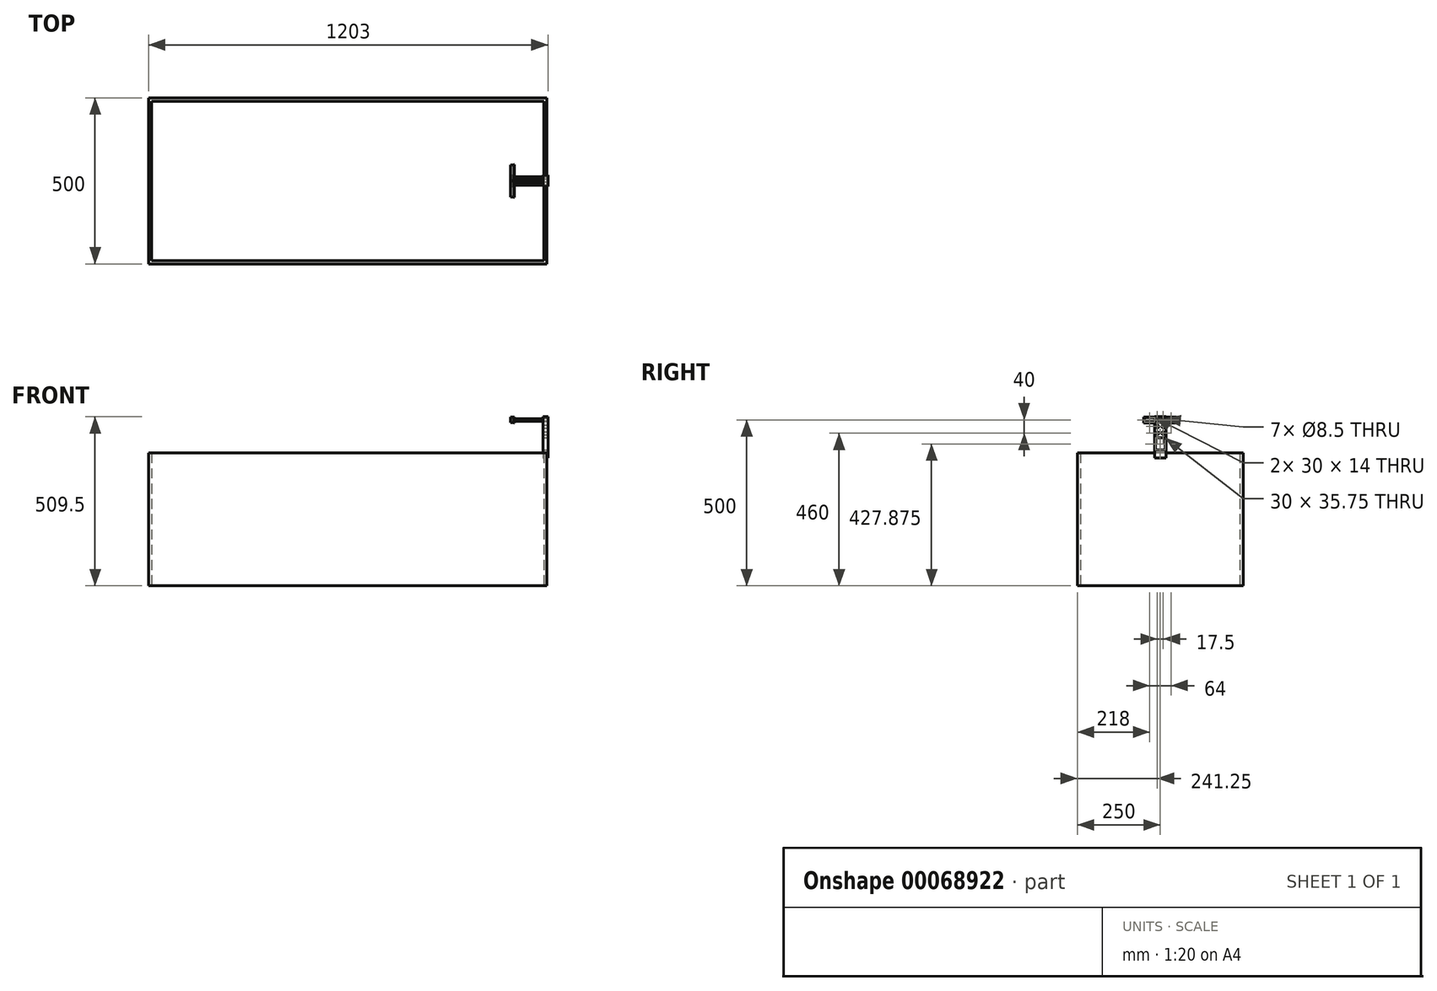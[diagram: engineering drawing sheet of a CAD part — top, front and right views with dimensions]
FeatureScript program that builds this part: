
annotation { "Feature Type Name" : "Feature", "Feature Type Description" : "" }
export const myFeature = defineFeature(function(context is Context, id is Id, definition is map)
    precondition{}
    {
        {
            var Q0;
            Q0=qCreatedBy(makeId("Right.planeOp"),FACE);
            var sketch = newSketch(context, id + "F0", { "sketchPlane" : qUnion([Q0])});
            skLineSegment(sketch, "E0.rect.bottom", {"start": v(-49.5, 9) * mm, "end": v(49.5, 9) * mm});
            skLineSegment(sketch, "E0.rect.top", {"start": v(-49.5, -9) * mm, "end": v(49.5, -9) * mm});
            skLineSegment(sketch, "E0.rect.left", {"start": v(-49.5, 9) * mm, "end": v(-49.5, -9) * mm});
            skLineSegment(sketch, "E0.rect.right", {"start": v(49.5, 9) * mm, "end": v(49.5, -9) * mm});
            skLineSegment(sketch, "E1.bottom", {"start": v(-49.5, -9) * mm, "end": v(0, -9) * mm, "construction": true});
            skLineSegment(sketch, "E1.top", {"start": v(-49.5, 9) * mm, "end": v(0, 9) * mm, "construction": true});
            skLineSegment(sketch, "E2", {"start": v(0, 9) * mm, "end": v(0, -9) * mm, "construction": true});
            skPoint(sketch, "E3.middle", {"position": v(0, 0) * mm});
            skLineSegment(sketch, "E4.bottom", {"start": v(-48, 8) * mm, "end": v(-16, 8) * mm});
            skLineSegment(sketch, "E4.top", {"start": v(-48, -8) * mm, "end": v(-16, -8) * mm});
            skLineSegment(sketch, "E4.left", {"start": v(-48, 8) * mm, "end": v(-48, -8) * mm});
            skLineSegment(sketch, "E5.MirrorCS", {"start": v(48, 8) * mm, "end": v(48, -8) * mm});
            skLineSegment(sketch, "E6.MirrorCS", {"start": v(48, 8) * mm, "end": v(16, 8) * mm});
            skLineSegment(sketch, "E7.MirrorCS", {"start": v(48, -8) * mm, "end": v(16, -8) * mm});
            skLineSegment(sketch, "E8.bottom", {"start": v(50, 9.5) * mm, "end": v(-50, 9.5) * mm});
            skLineSegment(sketch, "E8.top", {"start": v(50, -9.5) * mm, "end": v(-50, -9.5) * mm});
            skLineSegment(sketch, "E8.left", {"start": v(50, 9.5) * mm, "end": v(50, -9.5) * mm});
            skLineSegment(sketch, "E8.right", {"start": v(-50, 9.5) * mm, "end": v(-50, -9.5) * mm});
            skCircle(sketch, "E9", {"center": v(-8.75, 0) * mm, "radius": 4.25 * mm});
            skCircle(sketch, "E10.MirrorC", {"center": v(8.75, 0) * mm, "radius": 4.25 * mm});
            skLineSegment(sketch, "E11.bottom", {"start": v(0.75, 9.5) * mm, "end": v(-0.75, 9.5) * mm});
            skLineSegment(sketch, "E11.top", {"start": v(0.75, -9.5) * mm, "end": v(-0.75, -9.5) * mm});
            skLineSegment(sketch, "E11.left", {"start": v(0.75, 9.5) * mm, "end": v(0.75, -9.5) * mm});
            skLineSegment(sketch, "E11.right", {"start": v(-0.75, 9.5) * mm, "end": v(-0.75, -9.5) * mm});
            skLineSegment(sketch, "E12.0", {"start": v(47, 7) * mm, "end": v(17, 7) * mm});
            skLineSegment(sketch, "E12.1", {"start": v(47, 7) * mm, "end": v(47, -7) * mm});
            skLineSegment(sketch, "E12.2", {"start": v(47, -7) * mm, "end": v(17, -7) * mm});
            skLineSegment(sketch, "E12.3", {"start": v(17, 7) * mm, "end": v(17, -7) * mm});
            skLineSegment(sketch, "E13.MirrorCS", {"start": v(-47, 7) * mm, "end": v(-17, 7) * mm});
            skLineSegment(sketch, "E14.MirrorCS", {"start": v(-17, 7) * mm, "end": v(-17, -7) * mm});
            skLineSegment(sketch, "E15.MirrorCS", {"start": v(-47, -7) * mm, "end": v(-17, -7) * mm});
            skLineSegment(sketch, "E16.MirrorCS", {"start": v(-47, 7) * mm, "end": v(-47, -7) * mm});
            skLineSegment(sketch, "E17.bottom", {"start": v(-13, -8) * mm, "end": v(13, -8) * mm});
            skLineSegment(sketch, "E17.top", {"start": v(-13, 8) * mm, "end": v(13, 8) * mm});
            skLineSegment(sketch, "E18", {"start": v(-16, -8) * mm, "end": v(-13, -8) * mm});
            skLineSegment(sketch, "E19", {"start": v(-16, 8) * mm, "end": v(-13, 8) * mm});
            skLineSegment(sketch, "E20", {"start": v(13, -8) * mm, "end": v(16, -8) * mm});
            skLineSegment(sketch, "E21", {"start": v(13, 8) * mm, "end": v(16, 8) * mm});
            skPoint(sketch, "E3.left.end.orphan", {"position": v(-13, -6) * mm});
            skPoint(sketch, "E22.trimOffspring.start.orphan", {"position": v(-13, 6) * mm});
            skPoint(sketch, "E3.right.end.orphan", {"position": v(13, -6) * mm});
            skPoint(sketch, "E3.right.start.orphan", {"position": v(13, 6) * mm});
            skSolve(sketch);
        }
        {
            var Q0;
            Q0=makeQuery(id+"F0.imprint","IMPRINT",FACE,{"disambiguationData":[TD([[makeQuery(id+"F0.imprint","IMPRINT",EDGE,{"derivedFrom":sQuery(id+"F0.wireOp",EDGE,"E0.rect.bottom")}),-1.0]])]});
            var Q1;
            Q1=makeQuery(id+"F0.imprint","IMPRINT",FACE,{"disambiguationData":[TD([[makeQuery(id+"F0.imprint","IMPRINT",EDGE,{"derivedFrom":sQuery(id+"F0.wireOp",EDGE,"E3.bottom")}),-1.0]])]});
            var Q2;
            {var subQ0=sQuery(id+"F0.wireOp",EDGE,"E11.right");var subQ1=sQuery(id+"F0.wireOp",EDGE,"E0.rect.top");var subQ2=makeQuery(id+"F0.imprint","INTERSECT",VERTEX,{"derivedFrom":[subQ1,subQ0]});Q2=makeQuery(id+"F0.imprint","IMPRINT",FACE,{"disambiguationData":[TD([[makeQuery(id+"F0.imprint","IMPRINT",EDGE,{"disambiguationData":[TD([[subQ2,-1.0]])],"derivedFrom":subQ1}),1.0]])]});}
            var Q3;
            {var subQ4=sQuery(id+"F0.wireOp",EDGE,"E0.rect.right");Q3=makeQuery(id+"F0.imprint","IMPRINT",FACE,{"disambiguationData":[TD([[makeQuery(id+"F0.imprint","IMPRINT",EDGE,{"derivedFrom":subQ4}),-1.0]])]});}
            var Q4;
            {var subQ0=sQuery(id+"F0.wireOp",EDGE,"E3.right");Q4=makeQuery(id+"F0.imprint","IMPRINT",FACE,{"disambiguationData":[TD([[makeQuery(id+"F0.imprint","IMPRINT",EDGE,{"derivedFrom":subQ0}),-1.0]])]});}
            var Q5;
            {var subQ5=sQuery(id+"F0.wireOp",EDGE,"E3.left");Q5=makeQuery(id+"F0.imprint","IMPRINT",FACE,{"disambiguationData":[TD([[makeQuery(id+"F0.imprint","IMPRINT",EDGE,{"derivedFrom":subQ5}),1.0]])]});}
            var Q6;
            {var subQ0=sQuery(id+"F0.wireOp",EDGE,"E0.rect.left");Q6=makeQuery(id+"F0.imprint","IMPRINT",FACE,{"disambiguationData":[TD([[makeQuery(id+"F0.imprint","IMPRINT",EDGE,{"derivedFrom":subQ0}),1.0]])]});}
            var Q7;
            {var subQ0=sQuery(id+"F0.wireOp",EDGE,"E17.top");var subQ1=sQuery(id+"F0.wireOp",EDGE,"E11.left");var subQ2=makeQuery(id+"F0.imprint","INTERSECT",VERTEX,{"derivedFrom":[subQ1,subQ0]});Q7=makeQuery(id+"F0.imprint","IMPRINT",FACE,{"disambiguationData":[TD([[makeQuery(id+"F0.imprint","IMPRINT",EDGE,{"disambiguationData":[TD([[subQ2,-1.0]])],"derivedFrom":subQ1}),-1.0]])]});}
            var Q8;
            Q8=makeQuery(id+"F0.imprint","IMPRINT",FACE,{"disambiguationData":[TD([[makeQuery(id+"F0.imprint","IMPRINT",EDGE,{"derivedFrom":sQuery(id+"F0.wireOp",EDGE,"E10.MirrorC")}),1.0]])]});
            extrude(context, id + "F1", {"entities" : qUnion([Q0, Q1, Q2, Q3, Q4, Q5, Q6, Q7, Q8]), "depth" : 2 * mm});
        }
        {
            var Q0;
            Q0=makeQuery(id+"F0.imprint","IMPRINT",FACE,{"disambiguationData":[TD([[makeQuery(id+"F0.imprint","IMPRINT",EDGE,{"derivedFrom":sQuery(id+"F0.wireOp",EDGE,"E4.bottom")}),-1.0]])]});
            var Q1;
            Q1=makeQuery(id+"F0.imprint","IMPRINT",FACE,{"disambiguationData":[TD([[makeQuery(id+"F0.imprint","IMPRINT",EDGE,{"derivedFrom":sQuery(id+"F0.wireOp",EDGE,"E5.MirrorCS")}),-1.0]])]});
            var Q2;
            {var subQ0=sQuery(id+"F0.wireOp",EDGE,"E3.right");Q2=makeQuery(id+"F0.imprint","IMPRINT",FACE,{"disambiguationData":[TD([[makeQuery(id+"F0.imprint","IMPRINT",EDGE,{"derivedFrom":subQ0}),-1.0]])]});}
            var Q3;
            {var subQ5=sQuery(id+"F0.wireOp",EDGE,"E3.left");Q3=makeQuery(id+"F0.imprint","IMPRINT",FACE,{"disambiguationData":[TD([[makeQuery(id+"F0.imprint","IMPRINT",EDGE,{"derivedFrom":subQ5}),1.0]])]});}
            var Q4;
            Q4=makeQuery(id+"F0.imprint","IMPRINT",FACE,{"disambiguationData":[TD([[makeQuery(id+"F0.imprint","IMPRINT",EDGE,{"derivedFrom":sQuery(id+"F0.wireOp",EDGE,"E10.MirrorC")}),1.0]])]});
            extrude(context, id + "F2", {"entities" : qUnion([Q0, Q1, Q2, Q3, Q4]), "operationType" : NewBodyOperationType.ADD, "oppositeDirection" : true, "depth" : 10 * mm, "hasSecondDirection" : true, "secondDirectionOppositeDirection" : false, "secondDirectionDepth" : 2 * mm});
        }
        {
            var Q0;
            Q0 = qSketchRegion(id + "F0", true);
            var Q1;
            Q1=sQuery(id+"F0.wireOp",EDGE,"E8.right");
            var Q2;
            Q2=sQuery(id+"F0.wireOp",EDGE,"E8.top");
            var Q3;
            Q3=sQuery(id+"F0.wireOp",EDGE,"E8.left");
            var Q4;
            Q4=sQuery(id+"F0.wireOp",EDGE,"E8.bottom");
            extrude(context, id + "F3", {"entities" : qUnion([Q0]), "bodyType" : ToolBodyType.SURFACE, "surfaceEntities" : qUnion([Q1, Q2, Q3, Q4]), "oppositeDirection" : true, "depth" : 1000 * mm});
        }
        {
            var Q0;
            Q0=qCreatedBy(makeId("Top.planeOp"),FACE);
            cPlane(context, id + "F4", {"entities" : qUnion([Q0]), "cplaneType" : CPlaneType.OFFSET, "offset" : 500 * mm, "oppositeDirection" : true, "width" : 150 * mm, "height" : 150 * mm});
        }
        {
            var Q0;
            Q0=qCreatedBy(id+"F4.planeOp",FACE);
            var sketch = newSketch(context, id + "F5", { "sketchPlane" : qUnion([Q0])});
            skLineSegment(sketch, "E23.0", {"start": v(-1100, 250) * mm, "end": v(100, 250) * mm});
            skLineSegment(sketch, "E24.0", {"start": v(-1090, 240) * mm, "end": v(-1090, -240) * mm});
            skLineSegment(sketch, "E25.0", {"start": v(-1100, 250) * mm, "end": v(-1100, -250) * mm});
            skLineSegment(sketch, "E26.0", {"start": v(-1100, -250) * mm, "end": v(100, -250) * mm});
            skLineSegment(sketch, "E27.0", {"start": v(-1090, -240) * mm, "end": v(90, -240) * mm});
            skLineSegment(sketch, "E28.0", {"start": v(100, 250) * mm, "end": v(100, -250) * mm});
            skLineSegment(sketch, "E29.0", {"start": v(90, 240) * mm, "end": v(90, -240) * mm});
            skLineSegment(sketch, "E30.0", {"start": v(-1090, 240) * mm, "end": v(90, 240) * mm});
            skSolve(sketch);
        }
        {
            var Q0;
            Q0 = qSketchRegion(id + "F5", true);
            extrude(context, id + "F6", {"entities" : qUnion([Q0]), "depth" : 400 * mm});
        }
        {
            var Q0;
            Q0=makeQuery(id+"F6.opExtrude","CAP_FACE",FACE,{"disambiguationData":[OSD([sQuery(id+"F5.wireOp",EDGE,"E23.0"),sQuery(id+"F5.wireOp",EDGE,"E24.0"),sQuery(id+"F5.wireOp",EDGE,"E25.0"),sQuery(id+"F5.wireOp",EDGE,"E26.0"),sQuery(id+"F5.wireOp",EDGE,"E27.0"),sQuery(id+"F5.wireOp",EDGE,"E28.0"),sQuery(id+"F5.wireOp",EDGE,"E29.0"),sQuery(id+"F5.wireOp",EDGE,"E30.0")])],"isStart":false});
            var sketch = newSketch(context, id + "F7", { "sketchPlane" : qUnion([Q0])});
            skLineSegment(sketch, "E31", {"start": v(0, 15) * mm, "end": v(90, 15) * mm, "construction": true});
            skLineSegment(sketch, "E32", {"start": v(0, -15) * mm, "end": v(90, -15) * mm, "construction": true});
            skLineSegment(sketch, "E33.bottom", {"start": v(90, 15) * mm, "end": v(101, 15) * mm});
            skLineSegment(sketch, "E33.top", {"start": v(90, -15) * mm, "end": v(101, -15) * mm});
            skLineSegment(sketch, "E33.left", {"start": v(90, 15) * mm, "end": v(90, -15) * mm});
            skLineSegment(sketch, "E33.right", {"start": v(101, 15) * mm, "end": v(101, -15) * mm});
            skLineSegment(sketch, "E34.0", {"start": v(88, 17) * mm, "end": v(103, 17) * mm});
            skLineSegment(sketch, "E34.1", {"start": v(88, 17) * mm, "end": v(88, -17) * mm});
            skLineSegment(sketch, "E34.2", {"start": v(88, -17) * mm, "end": v(103, -17) * mm});
            skLineSegment(sketch, "E34.3", {"start": v(103, 17) * mm, "end": v(103, -17) * mm});
            skLineSegment(sketch, "E35", {"start": v(90, 15) * mm, "end": v(90, 17) * mm});
            skLineSegment(sketch, "E36", {"start": v(101, 15) * mm, "end": v(101, 17) * mm});
            skLineSegment(sketch, "E37", {"start": v(90, -15) * mm, "end": v(90, -17) * mm});
            skLineSegment(sketch, "E38", {"start": v(101, -15) * mm, "end": v(101, -17) * mm});
            skLineSegment(sketch, "E39", {"start": v(0, 0) * mm, "end": v(105.96, 0) * mm, "construction": true});
            skLineSegment(sketch, "E40", {"start": v(103, 0) * mm, "end": v(88, 0) * mm, "construction": true});
            skSolve(sketch);
        }
        {
            var Q0;
            Q0=makeQuery(id+"F7.imprint","IMPRINT",FACE,{"disambiguationData":[TD([[makeQuery(id+"F7.imprint","IMPRINT",EDGE,{"derivedFrom":sQuery(id+"F7.wireOp",EDGE,"E33.right")}),1.0]])]});
            var Q1;
            Q1=makeQuery(id+"F7.imprint","IMPRINT",FACE,{"disambiguationData":[TD([[makeQuery(id+"F7.imprint","IMPRINT",EDGE,{"derivedFrom":sQuery(id+"F7.wireOp",EDGE,"E33.left")}),-1.0]])]});
            var Q2;
            {var subQ0=sQuery(id+"F7.wireOp",EDGE,"E35");Q2=makeQuery(id+"F7.imprint","IMPRINT",FACE,{"disambiguationData":[TD([[makeQuery(id+"F7.imprint","IMPRINT",EDGE,{"derivedFrom":subQ0}),1.0]])]});}
            var Q3;
            {var subQ0=sQuery(id+"F7.wireOp",EDGE,"E36");Q3=makeQuery(id+"F7.imprint","IMPRINT",FACE,{"disambiguationData":[TD([[makeQuery(id+"F7.imprint","IMPRINT",EDGE,{"derivedFrom":subQ0}),1.0]])]});}
            var Q4;
            {var subQ0=sQuery(id+"F7.wireOp",EDGE,"E38");Q4=makeQuery(id+"F7.imprint","IMPRINT",FACE,{"disambiguationData":[TD([[makeQuery(id+"F7.imprint","IMPRINT",EDGE,{"derivedFrom":subQ0}),-1.0]])]});}
            var Q5;
            {var subQ0=sQuery(id+"F7.wireOp",EDGE,"E37");Q5=makeQuery(id+"F7.imprint","IMPRINT",FACE,{"disambiguationData":[TD([[makeQuery(id+"F7.imprint","IMPRINT",EDGE,{"derivedFrom":subQ0}),1.0]])]});}
            var Q6;
            {var subQ0=sQuery(id+"F7.wireOp",EDGE,"E33.right");Q6=makeQuery(id+"F7.imprint","IMPRINT",FACE,{"disambiguationData":[TD([[makeQuery(id+"F7.imprint","IMPRINT",EDGE,{"derivedFrom":subQ0}),-1.0]])]});}
            var Q7;
            {var subQ0=sQuery(id+"F7.wireOp",EDGE,"E33.left");Q7=makeQuery(id+"F7.imprint","IMPRINT",FACE,{"disambiguationData":[TD([[makeQuery(id+"F7.imprint","IMPRINT",EDGE,{"derivedFrom":subQ0}),1.0]])]});}
            extrude(context, id + "F8", {"entities" : qUnion([Q0, Q1, Q2, Q3, Q4, Q5, Q6, Q7]), "depth" : 10 * mm});
        }
        {
            var Q0;
            Q0=makeQuery(id+"F7.imprint","IMPRINT",FACE,{"disambiguationData":[TD([[makeQuery(id+"F7.imprint","IMPRINT",EDGE,{"derivedFrom":sQuery(id+"F7.wireOp",EDGE,"E33.left")}),-1.0]])]});
            var Q1;
            Q1=makeQuery(id+"F7.imprint","IMPRINT",FACE,{"disambiguationData":[TD([[makeQuery(id+"F7.imprint","IMPRINT",EDGE,{"derivedFrom":sQuery(id+"F7.wireOp",EDGE,"E33.right")}),1.0]])]});
            extrude(context, id + "F9", {"entities" : qUnion([Q0, Q1]), "operationType" : NewBodyOperationType.ADD, "oppositeDirection" : true, "depth" : 15 * mm});
        }
        {
            var Q0;
            {var subQ0=sQuery(id+"F7.wireOp",EDGE,"E34.3");Q0=makeQuery(id+"F9.boolean.opBoolean","MERGE",FACE,{"derivedFrom":[makeQuery(id+"F8.opExtrude","SWEPT_FACE",FACE,{"disambiguationData":[OSD([subQ0])]}),makeQuery(id+"F9.opExtrude","SWEPT_FACE",FACE,{"disambiguationData":[OSD([subQ0])]})]});}
            var sketch = newSketch(context, id + "F10", { "sketchPlane" : qUnion([Q0])});
            skLineSegment(sketch, "E41.0", {"start": v(-17, -90) * mm, "end": v(-17, -115) * mm});
            skLineSegment(sketch, "E42.0", {"start": v(17, -90) * mm, "end": v(17, -115) * mm});
            skLineSegment(sketch, "E43.0", {"start": v(17, -90) * mm, "end": v(-17, -90) * mm});
            skLineSegment(sketch, "E44.0", {"start": v(17, -100) * mm, "end": v(-17, -100) * mm});
            skCircle(sketch, "E45.0", {"center": v(-8.75, 0) * mm, "radius": 4.25 * mm});
            skCircle(sketch, "E46.0", {"center": v(8.75, 0) * mm, "radius": 4.25 * mm});
            skLineSegment(sketch, "E47.bottom", {"start": v(-17, -90) * mm, "end": v(17, -90) * mm});
            skLineSegment(sketch, "E47.top", {"start": v(-17, 9.5) * mm, "end": v(17, 9.5) * mm});
            skLineSegment(sketch, "E47.left", {"start": v(-17, -90) * mm, "end": v(-17, 9.5) * mm});
            skLineSegment(sketch, "E47.right", {"start": v(17, -90) * mm, "end": v(17, 9.5) * mm});
            skLineSegment(sketch, "E48", {"start": v(-8.98, -10) * mm, "end": v(11.55, -10) * mm, "construction": true});
            skCircle(sketch, "E49.MirrorC", {"center": v(-8.75, -20) * mm, "radius": 4.25 * mm});
            skCircle(sketch, "E50.MirrorC", {"center": v(8.75, -20) * mm, "radius": 4.25 * mm});
            skLineSegment(sketch, "E51", {"start": v(-8.28, -30) * mm, "end": v(12.94, -30) * mm});
            skCircle(sketch, "E52.MirrorC", {"center": v(8.75, -40) * mm, "radius": 4.25 * mm});
            skCircle(sketch, "E53.MirrorC", {"center": v(-8.75, -40) * mm, "radius": 4.25 * mm});
            skLineSegment(sketch, "E54.bottom", {"start": v(-15, -54.25) * mm, "end": v(15, -54.25) * mm});
            skLineSegment(sketch, "E54.top", {"start": v(-15, -90) * mm, "end": v(15, -90) * mm});
            skLineSegment(sketch, "E54.left", {"start": v(-15, -54.25) * mm, "end": v(-15, -90) * mm});
            skLineSegment(sketch, "E54.right", {"start": v(15, -54.25) * mm, "end": v(15, -90) * mm});
            skLineSegment(sketch, "E55.0", {"start": v(50, 9.5) * mm, "end": v(-50, 9.5) * mm});
            skSolve(sketch);
        }
        {
            var Q0;
            Q0 = qSketchRegion(id + "F10", true);
            var Q1;
            Q1=makeQuery(id+"F10.imprint","IMPRINT",FACE,{"disambiguationData":[TD([[makeQuery(id+"F10.imprint","IMPRINT",EDGE,{"derivedFrom":sQuery(id+"F10.wireOp",EDGE,"E45.0")}),-1.0]])]});
            extrude(context, id + "F11", {"entities" : qUnion([Q0, Q1]), "operationType" : NewBodyOperationType.ADD, "oppositeDirection" : true, "depth" : 15 * mm});
        }
        {
            var Q0;
            Q0=qCreatedBy(makeId("Top.planeOp"),FACE);
            var sketch = newSketch(context, id + "F12", { "sketchPlane" : qUnion([Q0])});
            skLineSegment(sketch, "E56.bottom", {"start": v(-7, -4.5) * mm, "end": v(103, -4.5) * mm});
            skLineSegment(sketch, "E56.top", {"start": v(-7, -8.5) * mm, "end": v(103, -8.5) * mm});
            skLineSegment(sketch, "E56.left", {"start": v(-7, -4.5) * mm, "end": v(-7, -8.5) * mm});
            skLineSegment(sketch, "E56.right", {"start": v(103, -4.5) * mm, "end": v(103, -8.5) * mm});
            skLineSegment(sketch, "E57", {"start": v(0, 0) * mm, "end": v(122.29, 0) * mm, "construction": true});
            skLineSegment(sketch, "E58.MirrorCS", {"start": v(-7, 4.5) * mm, "end": v(-7, 8.5) * mm});
            skLineSegment(sketch, "E59.MirrorCS", {"start": v(103, 4.5) * mm, "end": v(103, 8.5) * mm});
            skLineSegment(sketch, "E60.MirrorCS", {"start": v(-7, 8.5) * mm, "end": v(103, 8.5) * mm});
            skLineSegment(sketch, "E61.MirrorCS", {"start": v(-7, 4.5) * mm, "end": v(103, 4.5) * mm});
            skLineSegment(sketch, "E62.0", {"start": v(103, 4.5) * mm, "end": v(103, 13) * mm});
            skLineSegment(sketch, "E63.0", {"start": v(103, -4.5) * mm, "end": v(103, -13) * mm});
            skSolve(sketch);
        }
        {
            var Q0;
            Q0=makeQuery(id+"F12.imprint","IMPRINT",FACE,{"disambiguationData":[TD([[makeQuery(id+"F12.imprint","IMPRINT",EDGE,{"derivedFrom":sQuery(id+"F12.wireOp",EDGE,"E56.bottom")}),-1.0]])]});
            var Q1;
            Q1=sQuery(id+"F12.wireOp",EDGE,"E56.top");
            revolve(context, id + "F13", {"entities" : qUnion([Q0]), "axis" : qUnion([Q1]), "revolveType" : RevolveType.FULL});
        }
        {
            var Q0;
            Q0=makeQuery(id+"F12.imprint","IMPRINT",FACE,{"disambiguationData":[TD([[makeQuery(id+"F12.imprint","IMPRINT",EDGE,{"derivedFrom":sQuery(id+"F12.wireOp",EDGE,"E59.MirrorCS")}),1.0]])]});
            var Q1;
            {var subQ0=sQuery(id+"F12.wireOp",EDGE,"E58.MirrorCS");Q1=makeQuery(id+"F12.imprint","IMPRINT",FACE,{"disambiguationData":[TD([[makeQuery(id+"F12.imprint","IMPRINT",EDGE,{"derivedFrom":subQ0}),-1.0]])]});}
            var Q2;
            Q2=sQuery(id+"F12.wireOp",EDGE,"E60.MirrorCS");
            revolve(context, id + "F14", {"entities" : qUnion([Q0, Q1]), "axis" : qUnion([Q2]), "revolveType" : RevolveType.FULL});
        }
    });
